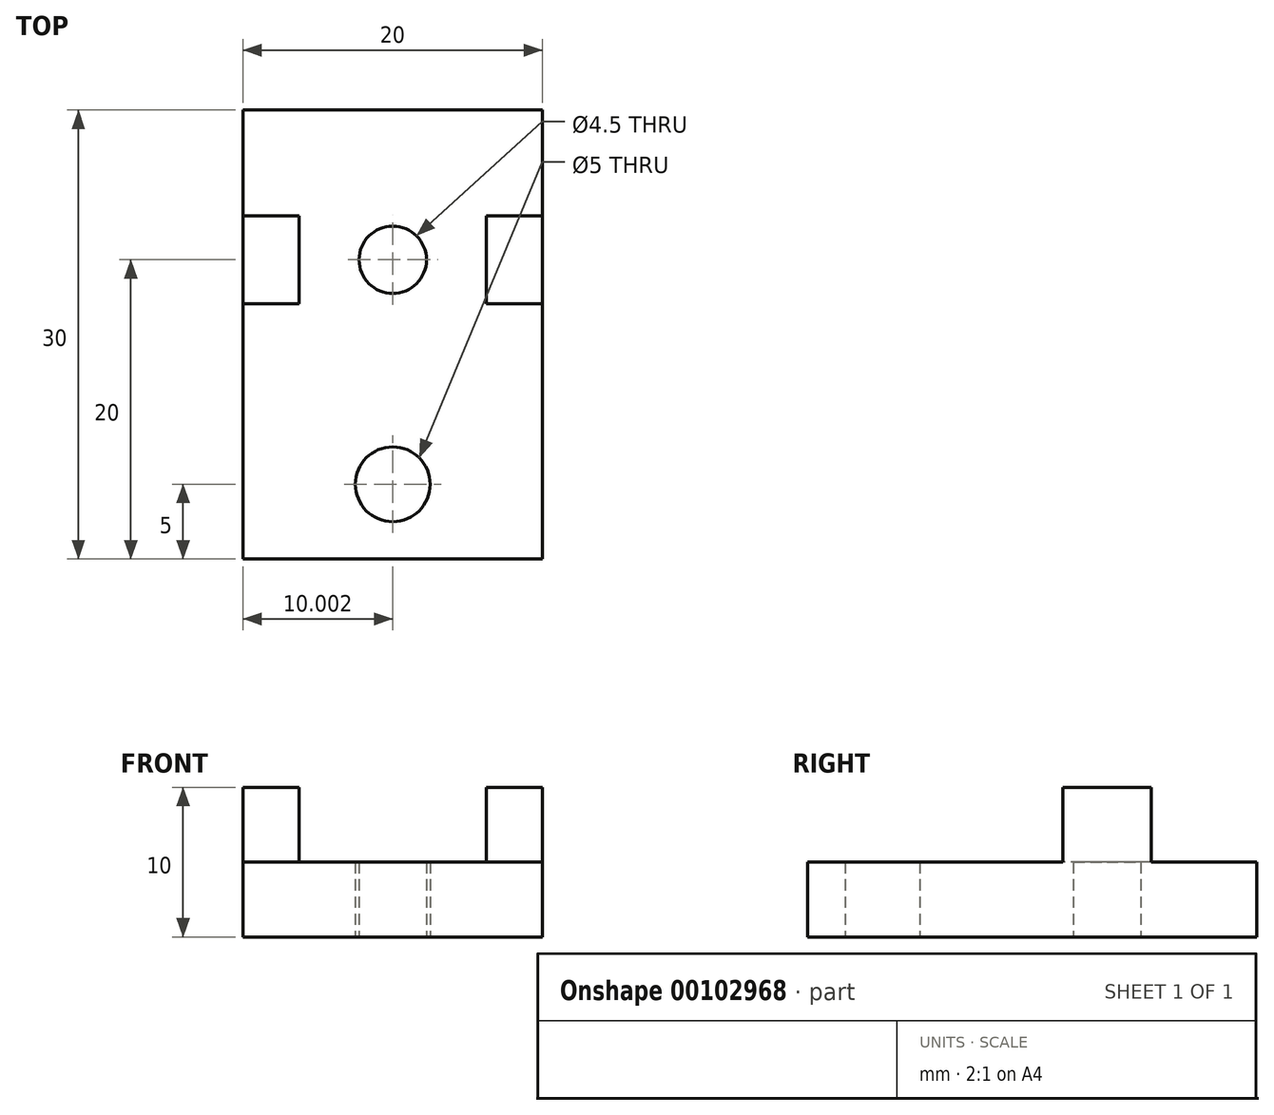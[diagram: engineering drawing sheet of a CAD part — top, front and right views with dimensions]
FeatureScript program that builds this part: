
annotation { "Feature Type Name" : "Feature", "Feature Type Description" : "" }
export const myFeature = defineFeature(function(context is Context, id is Id, definition is map)
    precondition{}
    {
        {
            var Q0;
            Q0=qCreatedBy(makeId("Top.planeOp"),FACE);
            var sketch = newSketch(context, id + "F0", { "sketchPlane" : qUnion([Q0])});
            skLineSegment(sketch, "E0.bottom", {"start": v(-18.76, 0) * mm, "end": v(1.24, 0) * mm});
            skLineSegment(sketch, "E0.top", {"start": v(-18.76, 30) * mm, "end": v(1.24, 30) * mm});
            skLineSegment(sketch, "E0.left", {"start": v(-18.76, 0) * mm, "end": v(-18.76, 30) * mm});
            skLineSegment(sketch, "E0.right", {"start": v(1.24, 0) * mm, "end": v(1.24, 30) * mm});
            skLineSegment(sketch, "E1", {"start": v(-18.76, 10) * mm, "end": v(1.24, 10) * mm});
            skCircle(sketch, "E2", {"center": v(-8.76, 5) * mm, "radius": 2.5 * mm});
            skCircle(sketch, "E3", {"center": v(-8.76, 20) * mm, "radius": 2.25 * mm});
            skPoint(sketch, "E4", {"position": v(-8.76, 30) * mm});
            skLineSegment(sketch, "E5.bottom", {"start": v(-18.76, 22.95) * mm, "end": v(-15, 22.95) * mm});
            skLineSegment(sketch, "E5.top", {"start": v(-18.76, 17.05) * mm, "end": v(-15, 17.05) * mm});
            skLineSegment(sketch, "E5.left", {"start": v(-18.76, 22.95) * mm, "end": v(-18.76, 17.05) * mm});
            skLineSegment(sketch, "E5.right", {"start": v(-15, 22.95) * mm, "end": v(-15, 17.05) * mm});
            skLineSegment(sketch, "E6.bottom", {"start": v(1.24, 22.95) * mm, "end": v(-2.5, 22.95) * mm});
            skLineSegment(sketch, "E6.top", {"start": v(1.24, 17.05) * mm, "end": v(-2.5, 17.05) * mm});
            skLineSegment(sketch, "E6.left", {"start": v(1.24, 22.95) * mm, "end": v(1.24, 17.05) * mm});
            skLineSegment(sketch, "E6.right", {"start": v(-2.5, 22.95) * mm, "end": v(-2.5, 17.05) * mm});
            skPoint(sketch, "E7", {"position": v(-15, 20) * mm});
            skSolve(sketch);
        }
        {
            var Q0;
            {var subQ3=sQuery(id+"F0.wireOp",EDGE,"E0.top");Q0=makeQuery(id+"F0.imprint","IMPRINT",FACE,{"disambiguationData":[TD([[makeQuery(id+"F0.imprint","IMPRINT",EDGE,{"derivedFrom":subQ3}),-1.0]])]});}
            var Q1;
            {var subQ1=sQuery(id+"F0.wireOp",EDGE,"E0.bottom");Q1=makeQuery(id+"F0.imprint","IMPRINT",FACE,{"disambiguationData":[TD([[makeQuery(id+"F0.imprint","IMPRINT",EDGE,{"derivedFrom":subQ1}),1.0]])]});}
            extrude(context, id + "F1", {"entities" : qUnion([Q0, Q1]), "depth" : 5 * mm});
        }
        {
            var Q0;
            {var subQ0=sQuery(id+"F0.wireOp",EDGE,"E5.bottom");Q0=makeQuery(id+"F0.imprint","IMPRINT",FACE,{"disambiguationData":[TD([[makeQuery(id+"F0.imprint","IMPRINT",EDGE,{"derivedFrom":subQ0}),-1.0]])]});}
            var Q1;
            {var subQ0=sQuery(id+"F0.wireOp",EDGE,"E6.bottom");Q1=makeQuery(id+"F0.imprint","IMPRINT",FACE,{"disambiguationData":[TD([[makeQuery(id+"F0.imprint","IMPRINT",EDGE,{"derivedFrom":subQ0}),1.0]])]});}
            extrude(context, id + "F2", {"entities" : qUnion([Q0, Q1]), "operationType" : NewBodyOperationType.ADD, "depth" : 10 * mm});
        }
    });
